# Revit family: Bola Sphere Flush
name_source: partatom
category: Lighting Fixtures
units: mm (PartAtom-declared; Revit-internal decimal feet)

## family parameters
Always vertical = Yes
Cut with Voids When Loaded = No
Light Source = Yes
OmniClass Number = 23.80.70.00
OmniClass Title = Lighting
Part Type = Normal
Room Calculation Point = No
Round Connector Dimension = Use Diameter
Shared = No
Work Plane-Based = No

## types (7) — shared parameters
Color Filter = 16777215
Default Elevation = 0' - 0"
Dimming Lamp Color Temperature Shift = <None>
ELEVATION FROM FLOOR = 4' - 0"
Emit Shape Visible in Rendering = No
Emit from Circle Diameter = 2' - 0"
Tilt Angle = 60.00°

## per-type parameters (varying)
| type | Photometric Web File |
| Bola Sphere Flush - 4 | BOLA 6W 4in Globe.IES |
| Bola Sphere Flush - 5 | BOLA 6W 5in Globe.IES |
| Bola Sphere Flush - 6 | BOLA 12W 6in Globe.IES |
| Bola Sphere Flush - 8 | BOLA 20W 8in_ 10in_ 12in Globe.IES |
| Bola Sphere Flush - 10 | BOLA 20W 8in_ 10in_ 12in Globe.IES |
| Bola Sphere Flush - 12 | BOLA 20W 8in_ 10in_ 12in Globe.IES |
| Bola Sphere Flush - 16 | BOLA 20W 8in_ 10in_ 12in Globe.IES |

type visibility flags: 7 boolean params named "<type name>" — each type sets only its own to Yes (folded from table)

## geometry (parser evidence)
native form markers: Sweep x3
no freeform markers — native parametric forms only
